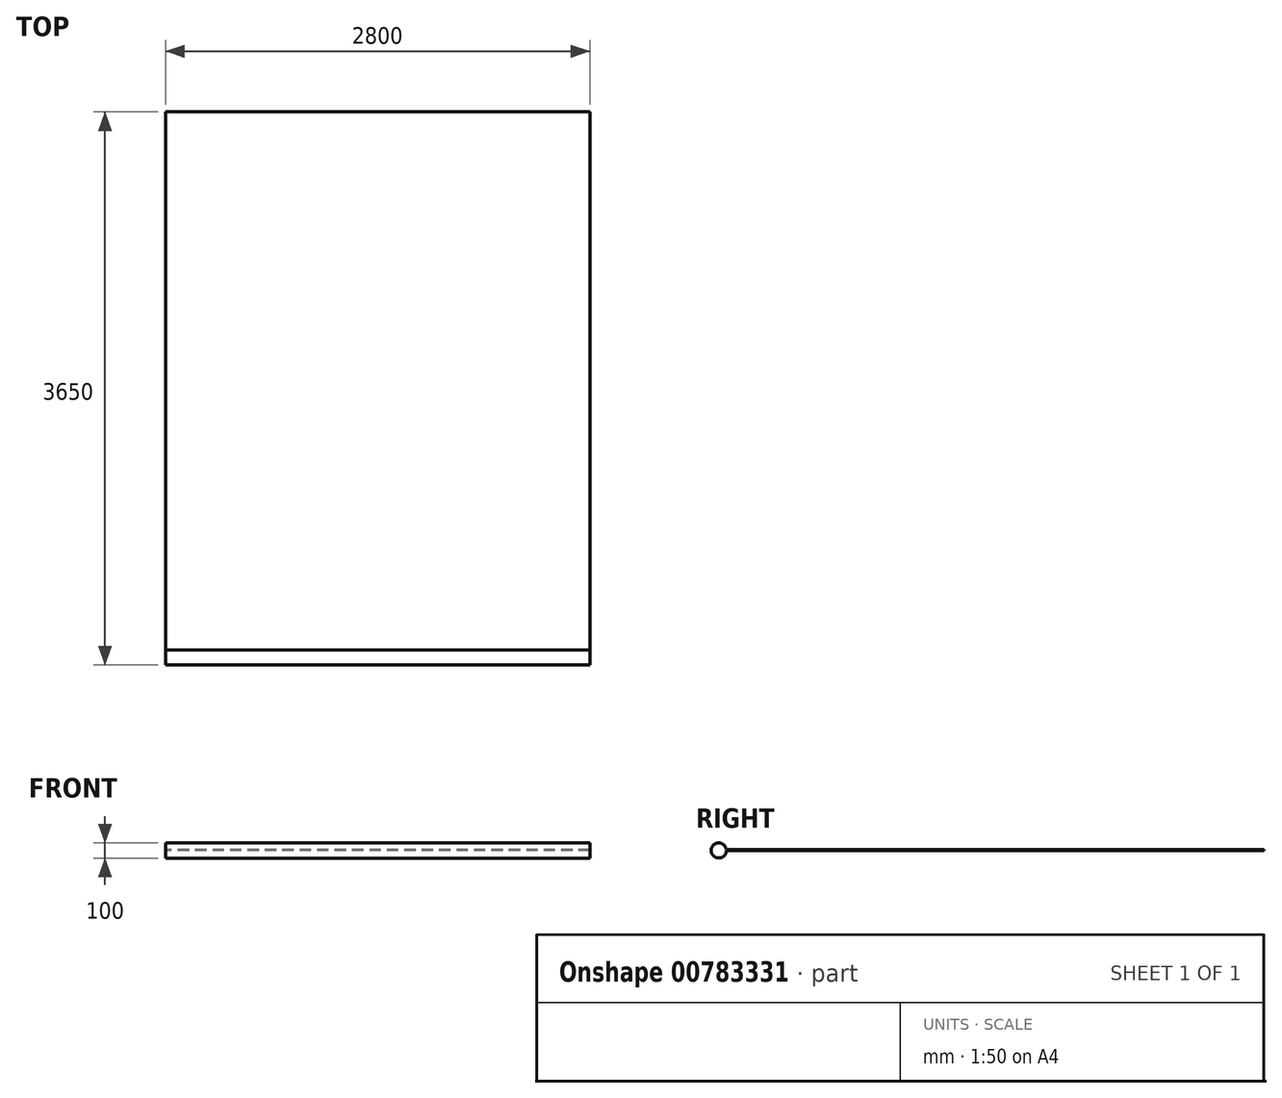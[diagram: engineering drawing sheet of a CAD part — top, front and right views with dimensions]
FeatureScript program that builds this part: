
annotation { "Feature Type Name" : "Feature", "Feature Type Description" : "" }
export const myFeature = defineFeature(function(context is Context, id is Id, definition is map)
    precondition{}
    {
        {
            var Q0;
            Q0=qCreatedBy(makeId("Top.planeOp"),FACE);
            var sketch = newSketch(context, id + "F0", { "sketchPlane" : qUnion([Q0])});
            skLineSegment(sketch, "E0.bottom", {"start": v(-1400, 0) * mm, "end": v(1400, 0) * mm});
            skLineSegment(sketch, "E0.top", {"start": v(-1400, 3600) * mm, "end": v(1400, 3600) * mm});
            skLineSegment(sketch, "E0.left", {"start": v(-1400, 0) * mm, "end": v(-1400, 3600) * mm});
            skLineSegment(sketch, "E0.right", {"start": v(1400, 0) * mm, "end": v(1400, 3600) * mm});
            skSolve(sketch);
        }
        {
            var Q0;
            Q0 = qSketchRegion(id + "F0", true);
            extrude(context, id + "F1", {"entities" : qUnion([Q0]), "depth" : 5 * mm, "offsetDistance" : 25 * mm});
        }
        {
            var Q0;
            Q0=qCreatedBy(makeId("Right.planeOp"),FACE);
            var sketch = newSketch(context, id + "F2", { "sketchPlane" : qUnion([Q0])});
            skCircle(sketch, "E1", {"center": v(0, 0) * mm, "radius": 50 * mm});
            skSolve(sketch);
        }
        {
            var Q0;
            Q0 = qSketchRegion(id + "F2", true);
            extrude(context, id + "F3", {"entities" : qUnion([Q0]), "operationType" : NewBodyOperationType.ADD, "endBound" : BoundingType.SYMMETRIC, "depth" : 2800 * mm, "offsetDistance" : 25 * mm});
        }
    });
